# Revit family: PD2-AP types Avec hôte
name_source: partatom
category: Dispositifs d'éclairage
units: mm (PartAtom-declared; Revit-internal decimal feet)

## family parameters
Conserver l'orientation des annotations = Oui
Cote de connecteur circulaire = Utiliser le diamètre
Couper avec des vides une fois chargée = Non
Hôte = Face
Partagée = Non
Point de calcul de pièce = Non
Type d'élément = Normal

## types (17) — shared parameters
Classe = II
Code d'assemblage = D5010200
Fabricant = B.E.G.
Hauteur de montage max = 300 cm
Image du type = 360°.jpg
Marque = LUXOMAT
Mode de pose = Saillie
URL = https://www.beg-luxomat.com
zero-valued in all types: Elévation par défaut

## per-type parameters (varying)
| type | Alimentation | Charge Cos ɸ =0.5 | Charge Cos ɸ =1 | Charge LED | Commentaires du type | Consommation | IP | Modèle | Relais | Référence | Température ambiante | Type de Sortie |
| 01- PD2-AP Générique | 110-240 V AC |  |  |  | DET.PRES.360°/Ø10M APPARENT |  | 20 ou 54 | PD2-AP |  |  | -25°C à +50°C |  |
| 02- PD2-M-1C-AP réf 92550 | 110-240 V AC | 1150 VA | 2300 W | 300 W | DET.PRES.MAITRE.1 CONTACT.360°/Ø10M APPARENT | 0,45 W | 20 ou 54 | PD2-M-1C-AP | 10 A | 92550 | -25°C à +50°C | TOR |
| 03- PD2-M-2C-AP réf 92150 | 110-240 V AC | 1150 VA | 2300 W | 300 W | DET.PRES.MAITRE.2 CONTACTS.360°/Ø10M APPARENT | 0,47 W | 20 ou 54 | PD2-M-2C-AP | 10 A / 3 A | 92150 | -25°C à +50°C | TOR + CVC |
| 06- PD2-M-DIM-AP réf 92153 | 110-240 V AC | 1150 VA | 2300 W | 300 W | DET.PRES.MAITRE.DIM(1-10V).360°/Ø10M APPARENT | 0,45 W | 20 ou 54 | PD2-M-DIM-AP | 10 A | 92153 | -25°C à +50°C | DIM (50 ballasts maxi) |
| 04- PD2N-M-DACO-AP réf 93452 | 110-240 V AC | 0 | 0 | 0 | DET.PRES.MAITRE.DALI 2.360°/Ø10M APPARENT + KIT AP réf 93454 | 2 W | 54 | PD2N-M-DACO-AP | 0 | 93452+93454 | -25°C à +50°C | DALI 2  (40 drivers maxi) |
| 05- PD2N-M-DACO-1C-AP réf 93455 | 110-240 V AC | 1150 VA | 2300 W | 300 W | DET.PRES.MAITRE.DALI 2 + CONTACT NO.360°/Ø10M APPARENT + KIT AP réf 93454 | 2 W | 54 | PD2N-M-DACO-1C-AP | 10 A | 93455+93454 | -25°C à +50°C | DALI 2 (40 drivers maxi) + Contact NO |
| 16- PD2-M-2C-11-48V-RR-AP réf 92305 | 11-48 V AC/DC | 0 | 0 | 0 | DET.PRES.MAITRE.11-48V.2 CONTACTS.RR.360°/Ø10M APPARENT | 0,76 W | 20 ou 54 | PD2-M-2C-11-48V-RR-AP | 100 mA | 92305 | -25°C à +50°C | Reed Relais |
| 17- PD2-M-2C-11-48V-3A-AP réf 92154 | 11-48 V AC/DC | 0 | 0 | 0 | DET.PRES.MAITRE.11-48V.2 CONTACTS.3A.360°/Ø10M APPARENT | 0,95 W | 20 ou 54 | PD2-M-2C-11-48V-3A-AP | 3 A | 92154 | -25°C à +50°C | TOR |
| 10- PD2N-KNX-BA-AP réf 93381 | 24 V DC par Bus KNX | 0 | 0 | 0 | DET.PRES.KNX.VERSION BASIQUE.360°/Ø10M ENCASTRE + KIT AP réf 93307 | 12 mA | 54 | PD2N-KNX-BA-AP | 0 | 93381+93307 | -5°C à +45°C | KNX - 1 sortie Eclairage TOR |
| 11- PD2N-KNX-ST-AP réf 93383 | 24 V DC par Bus KNX | 0 | 0 | 0 | DET.PRES.KNX.VERSION STANDARD.360°/Ø10M ENCASTRE + KIT AP réf 93307 | 12 mA | 54 | PD2N-KNX-ST-AP | 0 | 93383+93307 | -5°C à +45°C | KNX - 1 sortie Eclairage TOR ou GRADATION / 3 sorties Présence |
| 12- PD2N-KNX-DX-AP réf 93361 | 24 V DC par Bus KNX | 0 | 0 | 0 | DET.PRES.KNX.VERSION DELUXE.360°/Ø10M ENCASTRE + KIT AP réf 93307 | 12 mA | 54 | PD2N-KNX-DX-AP | 0 | 93361+93307 | -5°C à +45°C | KNX - 1 sortie Eclairage TOR ou GRADATION / 3 sorties Présence / Capteur de température et bruit |
| 15- PD2N-LON-AP réf 92734 | 24 V DC par Bus LON | 0 | 0 | 0 | DET.PRES.LON.360°/Ø10M APPARENT | 12 mA | 20 ou 54 | PD2N-LON-AP | 0 | 92734 | -5°C à +45°C | LON |
| 07- PD2-S-AP réf 92152 | 110-240 V AC | 0 | 0 | 0 | DET.PRES.ESCLAVE.360°/Ø10M APPARENT | 0,25 W | 20 ou 54 | PD2-S-AP | 10 A | 92152 | -25°C à +50°C | Esclave |
| 08- PD2N-DALISYS-AP réf 93368 | 10-22 V DC par Bus DALI | 0 | 0 | 0 | MULTI.CAPTEUR.PRES.DALISYS.360°/Ø10M ENCASTRE + KIT AP réf 93307 | 3 mA | 54 | PD2N-DALISYS-AP | 0 | 93368+93307 | -25°C a +55°C | DALI Adressable |
| 09- PD2N-BMS-DALI-2-AP réf 93544 | 10-22 V DC par Bus DALI | 0 | 0 | 0 | MULTI.CAPTEUR.PRES.BMS.DALI 2.360°/Ø10M ENCASTRE + KIT AP réf 93307 | 7 mA | 54 | PD2N-BMS-DALI-2-AP | 0 | 93544+93307 | -25°C a +55°C | DALI 2 Adressable - BMS |
| 13- PD2N-KNXs-ST-AP réf 93511 | 24 V DC par Bus KNX | 0 | 0 | 0 | DET.PRES.KNX Sécure.VERSION STANDARD.360°/Ø10M ENCASTRE + KIT AP réf 93307 | 12 mA | 54 | PD2N-KNXs-ST-AP | 0 | 93511+93307 | -5°C à +45°C | KNX Sécure - 1 sortie Eclairage TOR ou GRADATION / 3 sorties Présence / HCL |
| 14- PD2N-KNXs-DX-AP réf 93513 | 24 V DC par Bus KNX | 0 | 0 | 0 | DET.PRES.KNX Sécure.VERSION DELUXE.360°/Ø10M ENCASTRE + KIT AP réf 93307 | 12 mA | 54 | PD2N-KNXs-DX-AP | 0 | 93513+93307 | -5°C à +45°C | KNX Sécure - 1 sortie Eclairage TOR ou GRADATION / 3 sorties Présence / Capteur de température et bruit / HCL |
